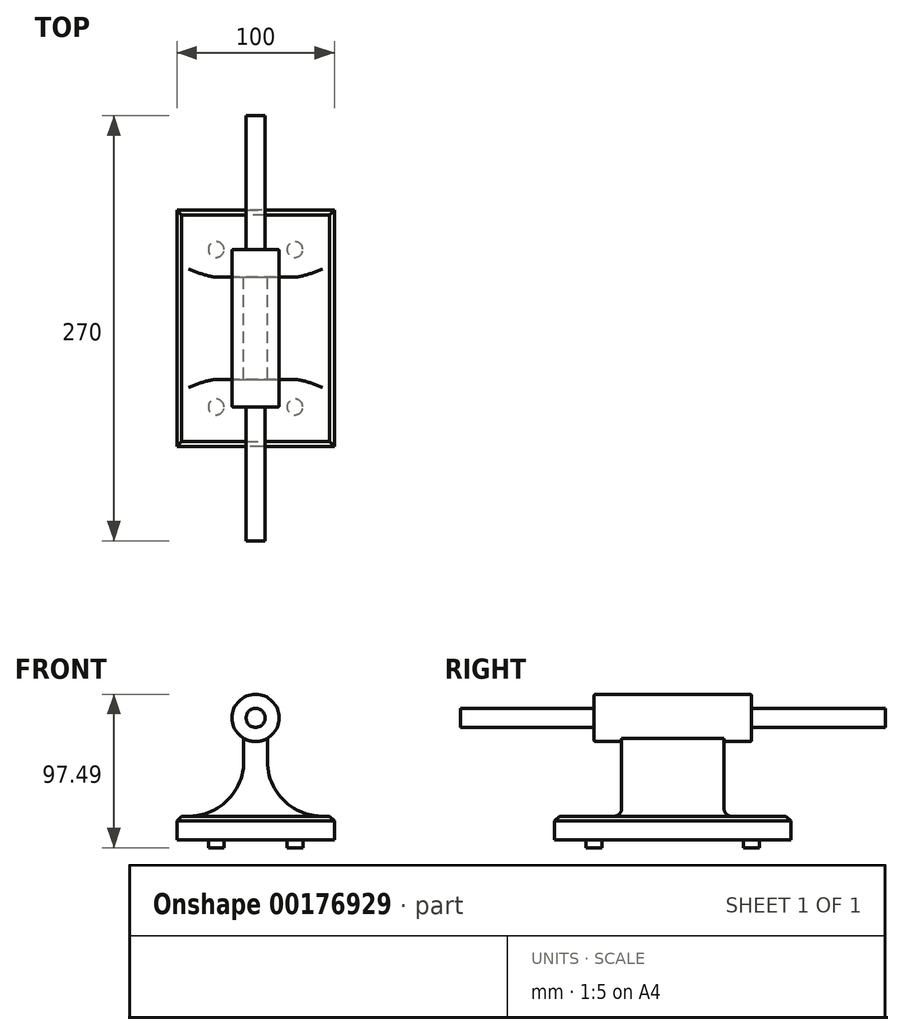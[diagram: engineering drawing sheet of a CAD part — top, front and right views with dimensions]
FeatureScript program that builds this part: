
annotation { "Feature Type Name" : "Feature", "Feature Type Description" : "" }
export const myFeature = defineFeature(function(context is Context, id is Id, definition is map)
    precondition{}
    {
        {
            var Q0;
            Q0=qCreatedBy(makeId("Front.planeOp"),FACE);
            var sketch = newSketch(context, id + "F0", { "sketchPlane" : qUnion([Q0])});
            skLineSegment(sketch, "E0.bottom", {"start": v(50, 7.5) * mm, "end": v(-50, 7.5) * mm});
            skLineSegment(sketch, "E0.top", {"start": v(50, -7.5) * mm, "end": v(27.5, -7.5) * mm});
            skLineSegment(sketch, "E0.left", {"start": v(50, 7.5) * mm, "end": v(50, -7.5) * mm});
            skLineSegment(sketch, "E0.right", {"start": v(-50, 7.5) * mm, "end": v(-50, -7.5) * mm});
            skPoint(sketch, "E0.middle", {"position": v(0, 0) * mm});
            skLineSegment(sketch, "E1.bottom", {"start": v(7.5, -60) * mm, "end": v(0, -60) * mm});
            skLineSegment(sketch, "E1.left", {"start": v(7.5, -47) * mm, "end": v(7.5, -27.5) * mm});
            skLineSegment(sketch, "E1.right", {"start": v(-7.5, -47) * mm, "end": v(-7.5, -27.5) * mm});
            skPoint(sketch, "E1.top.end.orphan", {"position": v(-7.5, 60) * mm});
            skPoint(sketch, "E1.top.start.orphan", {"position": v(7.5, 60) * mm});
            skPoint(sketch, "E2.newPointB", {"position": v(-50, -7.5) * mm});
            skArc(sketch, "E2.filletArc", {"start": v(27.5, -7.5) * mm, "mid": v(13.36, -13.36) * mm, "end": v(7.5, -27.5) * mm});
            skLineSegment(sketch, "E3", {"start": v(-27.5, -7.5) * mm, "end": v(-50, -7.5) * mm});
            skPoint(sketch, "E4.visualSharp", {"position": v(-7.5, -7.5) * mm});
            skArc(sketch, "E4.filletArc", {"start": v(-7.5, -27.5) * mm, "mid": v(-13.36, -13.36) * mm, "end": v(-27.5, -7.5) * mm});
            skCircle(sketch, "E5", {"center": v(0, -60) * mm, "radius": 15 * mm});
            skPoint(sketch, "E6.orphan", {"position": v(-7.5, -60) * mm});
            skLineSegment(sketch, "E7", {"start": v(-27.5, -7.5) * mm, "end": v(27.5, -7.5) * mm});
            skSolve(sketch);
        }
        {
            var Q0;
            Q0=makeQuery(id+"F0.imprint","IMPRINT",FACE,{"disambiguationData":[TD([[makeQuery(id+"F0.imprint","IMPRINT",EDGE,{"derivedFrom":sQuery(id+"F0.wireOp",EDGE,"E0.bottom")}),1.0]])]});
            extrude(context, id + "F1", {"entities" : qUnion([Q0]), "endBound" : BoundingType.SYMMETRIC, "depth" : 150 * mm});
        }
        {
            var Q0;
            Q0=qCreatedBy(makeId("Top.planeOp"),FACE);
            var sketch = newSketch(context, id + "F2", { "sketchPlane" : qUnion([Q0])});
            skLineSegment(sketch, "E8.bottom", {"start": v(7.5, -32.5) * mm, "end": v(-7.5, -32.5) * mm});
            skLineSegment(sketch, "E8.top", {"start": v(7.5, 32.5) * mm, "end": v(-7.5, 32.5) * mm});
            skLineSegment(sketch, "E8.left", {"start": v(7.5, -32.5) * mm, "end": v(7.5, 32.5) * mm});
            skLineSegment(sketch, "E8.right", {"start": v(-7.5, -32.5) * mm, "end": v(-7.5, 32.5) * mm});
            skPoint(sketch, "E8.middle", {"position": v(0, 0) * mm});
            skSolve(sketch);
        }
        {
            var Q0;
            Q0 = qSketchRegion(id + "F2", true);
            extrude(context, id + "F3", {"entities" : qUnion([Q0]), "operationType" : NewBodyOperationType.ADD, "depth" : 70 * mm});
        }
        {
            var Q0;
            Q0=qCreatedBy(makeId("Front.planeOp"),FACE);
            var sketch = newSketch(context, id + "F4", { "sketchPlane" : qUnion([Q0])});
            skCircle(sketch, "E9", {"center": v(0, 70) * mm, "radius": 15 * mm});
            skSolve(sketch);
        }
        {
            var Q0;
            Q0=makeQuery(id+"F4.imprint","IMPRINT",FACE,{"disambiguationData":[TD([[makeQuery(id+"F4.imprint","IMPRINT",EDGE,{"derivedFrom":sQuery(id+"F4.wireOp",EDGE,"E9")}),1.0]])]});
            extrude(context, id + "F5", {"entities" : qUnion([Q0]), "operationType" : NewBodyOperationType.ADD, "endBound" : BoundingType.SYMMETRIC, "depth" : 100 * mm});
        }
        {
            var Q0;
            Q0=makeQuery(id+"F5.opExtrude","CAP_FACE",FACE,{"disambiguationData":[OSD([sQuery(id+"F4.wireOp",EDGE,"E9")])],"isStart":true});
            var sketch = newSketch(context, id + "F6", { "sketchPlane" : qUnion([Q0])});
            skCircle(sketch, "E10", {"center": v(0, 70) * mm, "radius": 6 * mm});
            skSolve(sketch);
        }
        {
            var Q0;
            Q0=makeQuery(id+"F6.imprint","IMPRINT",FACE,{"disambiguationData":[TD([[makeQuery(id+"F6.imprint","IMPRINT",EDGE,{"derivedFrom":sQuery(id+"F6.wireOp",EDGE,"E10")}),1.0]])]});
            extrude(context, id + "F7", {"entities" : qUnion([Q0]), "operationType" : NewBodyOperationType.ADD, "depth" : 85 * mm});
        }
        {
            var Q0;
            Q0=makeQuery(id+"F5.opExtrude","CAP_FACE",FACE,{"disambiguationData":[OSD([sQuery(id+"F4.wireOp",EDGE,"E9")])],"isStart":false});
            var sketch = newSketch(context, id + "F8", { "sketchPlane" : qUnion([Q0])});
            skCircle(sketch, "E11", {"center": v(0, 70) * mm, "radius": 6 * mm});
            skSolve(sketch);
        }
        {
            var Q0;
            Q0 = qSketchRegion(id + "F8", true);
            extrude(context, id + "F9", {"entities" : qUnion([Q0]), "operationType" : NewBodyOperationType.ADD, "depth" : 85 * mm});
        }
        {
            var Q0;
            Q0=makeQuery(id+"F1.opExtrude","SWEPT_FACE",FACE,{"disambiguationData":[OSD([sQuery(id+"F0.wireOp",EDGE,"E0.top"),sQuery(id+"F0.wireOp",EDGE,"E3"),sQuery(id+"F0.wireOp",EDGE,"E7")])]});
            var sketch = newSketch(context, id + "F10", { "sketchPlane" : qUnion([Q0])});
            skCircle(sketch, "E12", {"center": v(-25, 50) * mm, "radius": 5 * mm});
            skCircle(sketch, "E13", {"center": v(25, 50) * mm, "radius": 5 * mm});
            skCircle(sketch, "E14", {"center": v(25, -50) * mm, "radius": 5 * mm});
            skCircle(sketch, "E15", {"center": v(-25, -50) * mm, "radius": 5 * mm});
            skSolve(sketch);
        }
        {
            var Q0;
            Q0=makeQuery(id+"F10.imprint","IMPRINT",FACE,{"disambiguationData":[TD([[makeQuery(id+"F10.imprint","IMPRINT",EDGE,{"derivedFrom":sQuery(id+"F10.wireOp",EDGE,"E12")}),1.0]])]});
            var Q1;
            Q1=makeQuery(id+"F10.imprint","IMPRINT",FACE,{"disambiguationData":[TD([[makeQuery(id+"F10.imprint","IMPRINT",EDGE,{"derivedFrom":sQuery(id+"F10.wireOp",EDGE,"E13")}),1.0]])]});
            var Q2;
            Q2=makeQuery(id+"F10.imprint","IMPRINT",FACE,{"disambiguationData":[TD([[makeQuery(id+"F10.imprint","IMPRINT",EDGE,{"derivedFrom":sQuery(id+"F10.wireOp",EDGE,"E15")}),1.0]])]});
            var Q3;
            Q3=makeQuery(id+"F10.imprint","IMPRINT",FACE,{"disambiguationData":[TD([[makeQuery(id+"F10.imprint","IMPRINT",EDGE,{"derivedFrom":sQuery(id+"F10.wireOp",EDGE,"E14")}),1.0]])]});
            extrude(context, id + "F11", {"entities" : qUnion([Q0, Q1, Q2, Q3]), "operationType" : NewBodyOperationType.ADD, "depth" : 5 * mm});
        }
        {
            var Q0;
            Q0=makeQuery(id+"F3.boolean.opBoolean","INTERSECT",EDGE,{"derivedFrom":[makeQuery(id+"F1.opExtrude","SWEPT_FACE",FACE,{"disambiguationData":[OSD([sQuery(id+"F0.wireOp",EDGE,"E0.bottom")])]}),makeQuery(id+"F3.opExtrude","SWEPT_FACE",FACE,{"disambiguationData":[OSD([sQuery(id+"F2.wireOp",EDGE,"E8.left")])]})]});
            var Q1;
            Q1=makeQuery(id+"F3.boolean.opBoolean","INTERSECT",EDGE,{"derivedFrom":[makeQuery(id+"F1.opExtrude","SWEPT_FACE",FACE,{"disambiguationData":[OSD([sQuery(id+"F0.wireOp",EDGE,"E0.bottom")])]}),makeQuery(id+"F3.opExtrude","SWEPT_FACE",FACE,{"disambiguationData":[OSD([sQuery(id+"F2.wireOp",EDGE,"E8.right")])]})]});
            fillet(context, id + "F12", {"entities" : qUnion([Q0, Q1]), "radius" : 35 * mm, "tangentPropagation" : true, "allowEdgeOverflow" : false});
        }
        {
            var Q0;
            Q0=makeQuery(id+"F3.boolean.opBoolean","INTERSECT",EDGE,{"derivedFrom":[makeQuery(id+"F1.opExtrude","SWEPT_FACE",FACE,{"disambiguationData":[OSD([sQuery(id+"F0.wireOp",EDGE,"E0.bottom")])]}),makeQuery(id+"F3.opExtrude","SWEPT_FACE",FACE,{"disambiguationData":[OSD([sQuery(id+"F2.wireOp",EDGE,"E8.bottom")])]})]});
            var Q1;
            Q1=makeQuery(id+"F3.boolean.opBoolean","INTERSECT",EDGE,{"derivedFrom":[makeQuery(id+"F1.opExtrude","SWEPT_FACE",FACE,{"disambiguationData":[OSD([sQuery(id+"F0.wireOp",EDGE,"E0.bottom")])]}),makeQuery(id+"F3.opExtrude","SWEPT_FACE",FACE,{"disambiguationData":[OSD([sQuery(id+"F2.wireOp",EDGE,"E8.top")])]})]});
            fillet(context, id + "F13", {"entities" : qUnion([Q0, Q1]), "radius" : 5 * mm, "tangentPropagation" : true, "allowEdgeOverflow" : false});
        }
        {
            var Q0;
            Q0=makeQuery(id+"F1.opExtrude","SWEPT_EDGE",EDGE,{"disambiguationData":[OSD([sQuery(id+"F0.wireOp",EDGE,"E0.bottom"),sQuery(id+"F0.wireOp",EDGE,"E0.right")])]});
            var Q1;
            Q1=makeQuery(id+"F1.opExtrude","CAP_EDGE",EDGE,{"disambiguationData":[OSD([sQuery(id+"F0.wireOp",EDGE,"E0.bottom")])],"isStart":true});
            var Q2;
            Q2=makeQuery(id+"F1.opExtrude","SWEPT_EDGE",EDGE,{"disambiguationData":[OSD([sQuery(id+"F0.wireOp",EDGE,"E0.bottom"),sQuery(id+"F0.wireOp",EDGE,"E0.left")])]});
            var Q3;
            Q3=makeQuery(id+"F1.opExtrude","CAP_EDGE",EDGE,{"disambiguationData":[OSD([sQuery(id+"F0.wireOp",EDGE,"E0.bottom")])],"isStart":false});
            chamfer(context, id + "F14", {"entities" : qUnion([Q0, Q1, Q2, Q3]), "width" : 3 * mm, "tangentPropagation" : true});
        }
        {
            var Q0;
            Q0=makeQuery(id+"F5.opExtrude","CAP_EDGE",EDGE,{"disambiguationData":[OSD([sQuery(id+"F4.wireOp",EDGE,"E9")])],"isStart":false});
            var Q1;
            Q1=makeQuery(id+"F5.opExtrude","CAP_EDGE",EDGE,{"disambiguationData":[OSD([sQuery(id+"F4.wireOp",EDGE,"E9")])],"isStart":true});
            fillet(context, id + "F15", {"entities" : qUnion([Q0, Q1]), "radius" : 1 * mm, "tangentPropagation" : true, "allowEdgeOverflow" : false});
        }
    });
